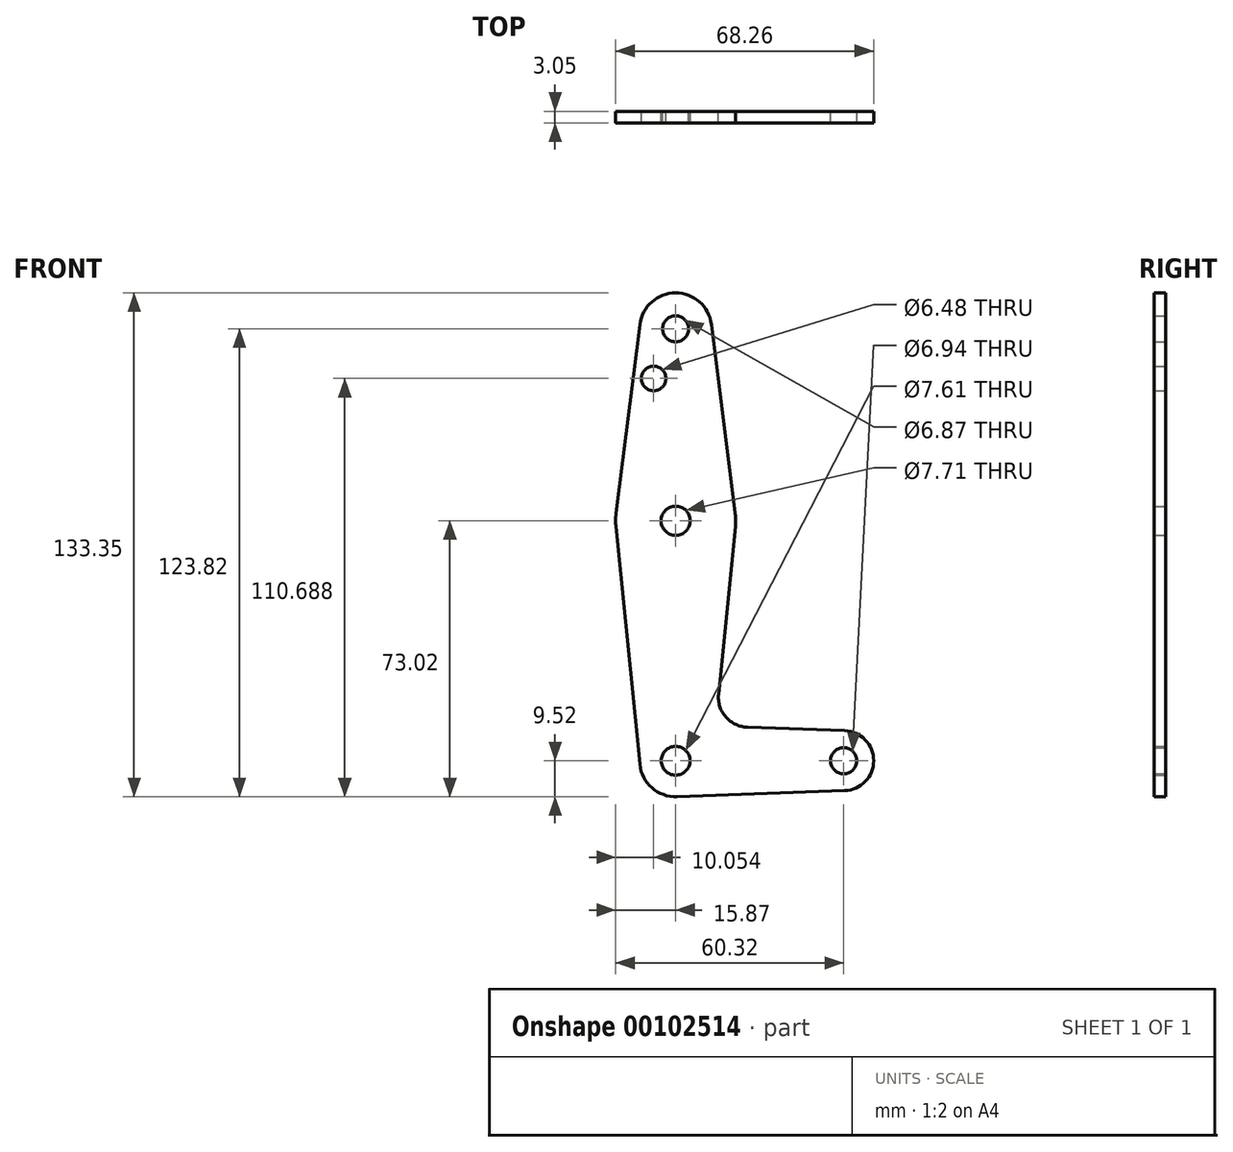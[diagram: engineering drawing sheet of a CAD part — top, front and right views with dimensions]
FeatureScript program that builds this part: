
annotation { "Feature Type Name" : "Feature", "Feature Type Description" : "" }
export const myFeature = defineFeature(function(context is Context, id is Id, definition is map)
    precondition{}
    {
        {
            var Q0;
            Q0=qCreatedBy(makeId("Front.planeOp"),FACE);
            var sketch = newSketch(context, id + "F0", { "sketchPlane" : qUnion([Q0])});
            skLineSegment(sketch, "E0", {"start": v(0, 114.3) * mm, "end": v(0, 0) * mm, "construction": true});
            skLineSegment(sketch, "E1", {"start": v(0, 0) * mm, "end": v(44.45, 0) * mm, "construction": true});
            skCircle(sketch, "E2", {"center": v(0, 114.3) * mm, "radius": 9.53 * mm});
            skCircle(sketch, "E3", {"center": v(0, 63.5) * mm, "radius": 15.88 * mm});
            skCircle(sketch, "E4", {"center": v(0, 0) * mm, "radius": 9.53 * mm});
            skCircle(sketch, "E5", {"center": v(44.45, 0) * mm, "radius": 7.94 * mm});
            skPoint(sketch, "E6", {"position": v(0, 57.15) * mm});
            skLineSegment(sketch, "E7", {"start": v(-9.45, 115.5) * mm, "end": v(-15.75, 65.48) * mm});
            skLineSegment(sketch, "E8", {"start": v(9.45, 115.5) * mm, "end": v(15.75, 65.48) * mm});
            skLineSegment(sketch, "E9", {"start": v(-15.8, 61.91) * mm, "end": v(-9.48, -0.95) * mm});
            skLineSegment(sketch, "E10", {"start": v(15.8, 61.91) * mm, "end": v(11.34, 17.6) * mm});
            skLineSegment(sketch, "E11", {"start": v(18.97, 8.85) * mm, "end": v(44.73, 7.93) * mm});
            skLineSegment(sketch, "E12", {"start": v(0.34, -9.52) * mm, "end": v(44.73, -7.93) * mm});
            skArc(sketch, "E13.filletArc", {"start": v(11.34, 17.6) * mm, "mid": v(13.26, 11.57) * mm, "end": v(18.97, 8.85) * mm});
            skCircle(sketch, "E14", {"center": v(0, 114.3) * mm, "radius": 3.44 * mm});
            skCircle(sketch, "E15", {"center": v(0, 63.5) * mm, "radius": 3.85 * mm});
            skCircle(sketch, "E16", {"center": v(0, 0) * mm, "radius": 3.8 * mm});
            skCircle(sketch, "E17", {"center": v(44.45, 0) * mm, "radius": 3.47 * mm});
            skCircle(sketch, "E18", {"center": v(-5.82, 101.17) * mm, "radius": 3.24 * mm});
            skSolve(sketch);
        }
        {
            var Q0;
            Q0 = qSketchRegion(id + "F0", true);
            extrude(context, id + "F1", {"entities" : qUnion([Q0]), "depth" : 3.05 * mm});
        }
    });
